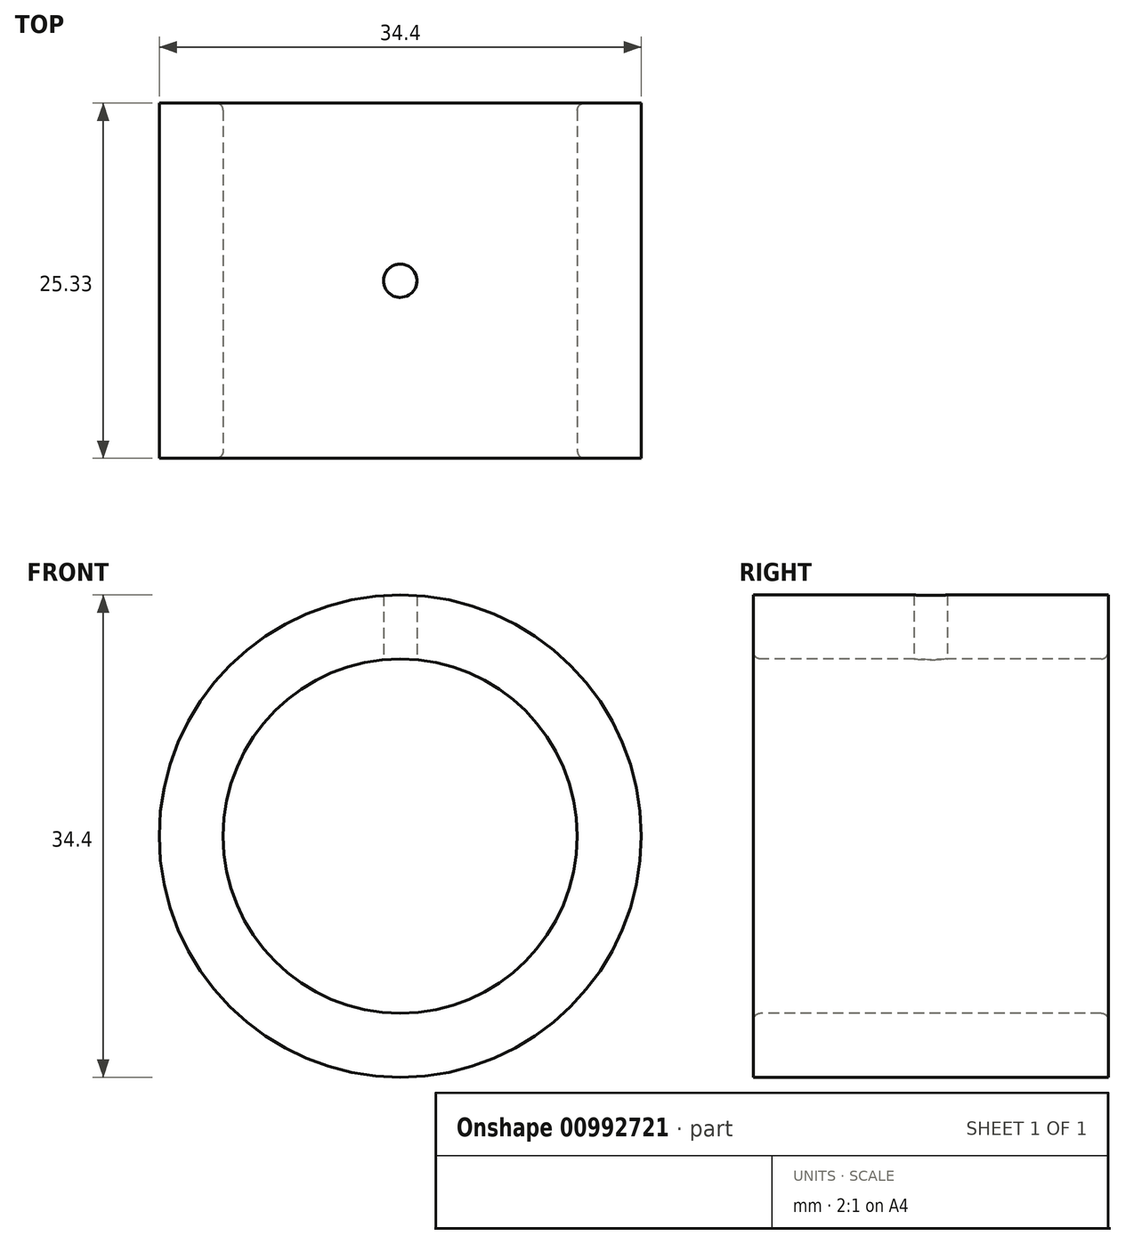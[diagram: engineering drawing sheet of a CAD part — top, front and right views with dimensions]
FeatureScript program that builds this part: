
annotation { "Feature Type Name" : "Feature", "Feature Type Description" : "" }
export const myFeature = defineFeature(function(context is Context, id is Id, definition is map)
    precondition{}
    {
        {
            var Q0;
            Q0=qCreatedBy(makeId("Top.planeOp"),FACE);
            var sketch = newSketch(context, id + "F0", { "sketchPlane" : qUnion([Q0])});
            skLineSegment(sketch, "E0", {"start": v(0, 0) * mm, "end": v(17.4, 0) * mm, "construction": true});
            skCircle(sketch, "E1", {"center": v(0, 0) * mm, "radius": 8.9 * mm, "construction": true});
            skLineSegment(sketch, "E2", {"start": v(17.4, 12.66) * mm, "end": v(13.14, 12.66) * mm});
            skLineSegment(sketch, "E3", {"start": v(17.4, -12.66) * mm, "end": v(13.14, -12.66) * mm});
            skLineSegment(sketch, "E4", {"start": v(0, -15.82) * mm, "end": v(0, 21.52) * mm, "construction": true});
            skLineSegment(sketch, "E5.0", {"start": v(17.4, -14.16) * mm, "end": v(11.14, -14.16) * mm});
            skLineSegment(sketch, "E5.2", {"start": v(17.4, 14.17) * mm, "end": v(11.14, 14.17) * mm});
            skLineSegment(sketch, "E6", {"start": v(17.4, 14.17) * mm, "end": v(17.4, 12.66) * mm});
            skLineSegment(sketch, "E7", {"start": v(17.4, -12.66) * mm, "end": v(17.4, -14.16) * mm});
            skLineSegment(sketch, "E8", {"start": v(11.14, 14.17) * mm, "end": v(11.14, -14.16) * mm});
            skLineSegment(sketch, "E9", {"start": v(12.64, 12.16) * mm, "end": v(12.64, -12.16) * mm});
            skPoint(sketch, "E10.visualSharp", {"position": v(12.64, 12.66) * mm});
            skArc(sketch, "E10.filletArc", {"start": v(13.14, 12.66) * mm, "mid": v(12.78, 12.52) * mm, "end": v(12.64, 12.16) * mm});
            skPoint(sketch, "E11.visualSharp", {"position": v(12.64, -12.66) * mm});
            skArc(sketch, "E11.filletArc", {"start": v(12.64, -12.16) * mm, "mid": v(12.78, -12.5) * mm, "end": v(13.14, -12.66) * mm});
            skPoint(sketch, "E12.visualSharp", {"position": v(11.14, 14.17) * mm});
            skPoint(sketch, "E13.visualSharp", {"position": v(11.14, -14.16) * mm});
            skSolve(sketch);
        }
        {
            var Q0;
            Q0=qSketchRegion(id+"F0",true);
            var Q1;
            Q1=sQuery(id+"F0.wireOp",EDGE,"E4");
            revolve(context, id + "F1", {"entities" : qUnion([Q0]), "axis" : qUnion([Q1]), "revolveType" : RevolveType.FULL});
        }
        {
            var Q0;
            Q0=qCreatedBy(makeId("Front.planeOp"),FACE);
            var sketch = newSketch(context, id + "F2", { "sketchPlane" : qUnion([Q0])});
            skCircle(sketch, "E14.0", {"center": v(0, 0) * mm, "radius": 12.64 * mm});
            skCircle(sketch, "E15.0", {"center": v(0, 0) * mm, "radius": 17.4 * mm, "construction": true});
            skCircle(sketch, "E16", {"center": v(0, 0) * mm, "radius": 17.2 * mm});
            skSolve(sketch);
        }
        {
            var Q0;
            Q0=qSketchRegion(id+"F2",true);
            extrude(context, id + "F3", {"entities" : qUnion([Q0]), "endBound" : BoundingType.UP_TO_NEXT, "oppositeDirection" : true, "depth" : 25.4 * mm, "offsetDistance" : 25.4 * mm, "hasSecondDirection" : true, "secondDirectionBound" : SecondDirectionBoundingType.UP_TO_NEXT, "secondDirectionOppositeDirection" : false, "secondDirectionDepth" : 25.4 * mm});
        }
        {
            var Q0;
            Q0=makeQuery(id+"F1.opRevolve","SWEPT_BODY",BODY,{"disambiguationData":[OSD([sQuery(id+"F0.wireOp",EDGE,"E2"),sQuery(id+"F0.wireOp",EDGE,"E3"),sQuery(id+"F0.wireOp",EDGE,"E5.0"),sQuery(id+"F0.wireOp",EDGE,"E5.2"),sQuery(id+"F0.wireOp",EDGE,"E6"),sQuery(id+"F0.wireOp",EDGE,"E7"),sQuery(id+"F0.wireOp",EDGE,"E8"),sQuery(id+"F0.wireOp",EDGE,"E9"),sQuery(id+"F0.wireOp",EDGE,"E10.filletArc"),sQuery(id+"F0.wireOp",EDGE,"E11.filletArc")])]});
            var Q1;
            Q1=makeQuery(id+"F3.opExtrude","SWEPT_BODY",BODY,{"disambiguationData":[OSD([sQuery(id+"F2.wireOp",EDGE,"E14.0"),sQuery(id+"F2.wireOp",EDGE,"E15.0")])]});
            booleanBodies(context, id + "F4", {"operationType" : BooleanOperationType.SUBTRACTION, "tools" : qUnion([Q0]), "targets" : qUnion([Q1])});
        }
        {
            var Q0;
            Q0=qCreatedBy(makeId("Top.planeOp"),FACE);
            var sketch = newSketch(context, id + "F5", { "sketchPlane" : qUnion([Q0])});
            skCircle(sketch, "E17", {"center": v(0, 0) * mm, "radius": 1.2 * mm});
            skSolve(sketch);
        }
        {
            var Q0;
            Q0=qSketchRegion(id+"F5",true);
            extrude(context, id + "F6", {"entities" : qUnion([Q0]), "operationType" : NewBodyOperationType.REMOVE, "endBound" : BoundingType.THROUGH_ALL, "depth" : 25.4 * mm, "offsetDistance" : 25.4 * mm});
        }
    });
